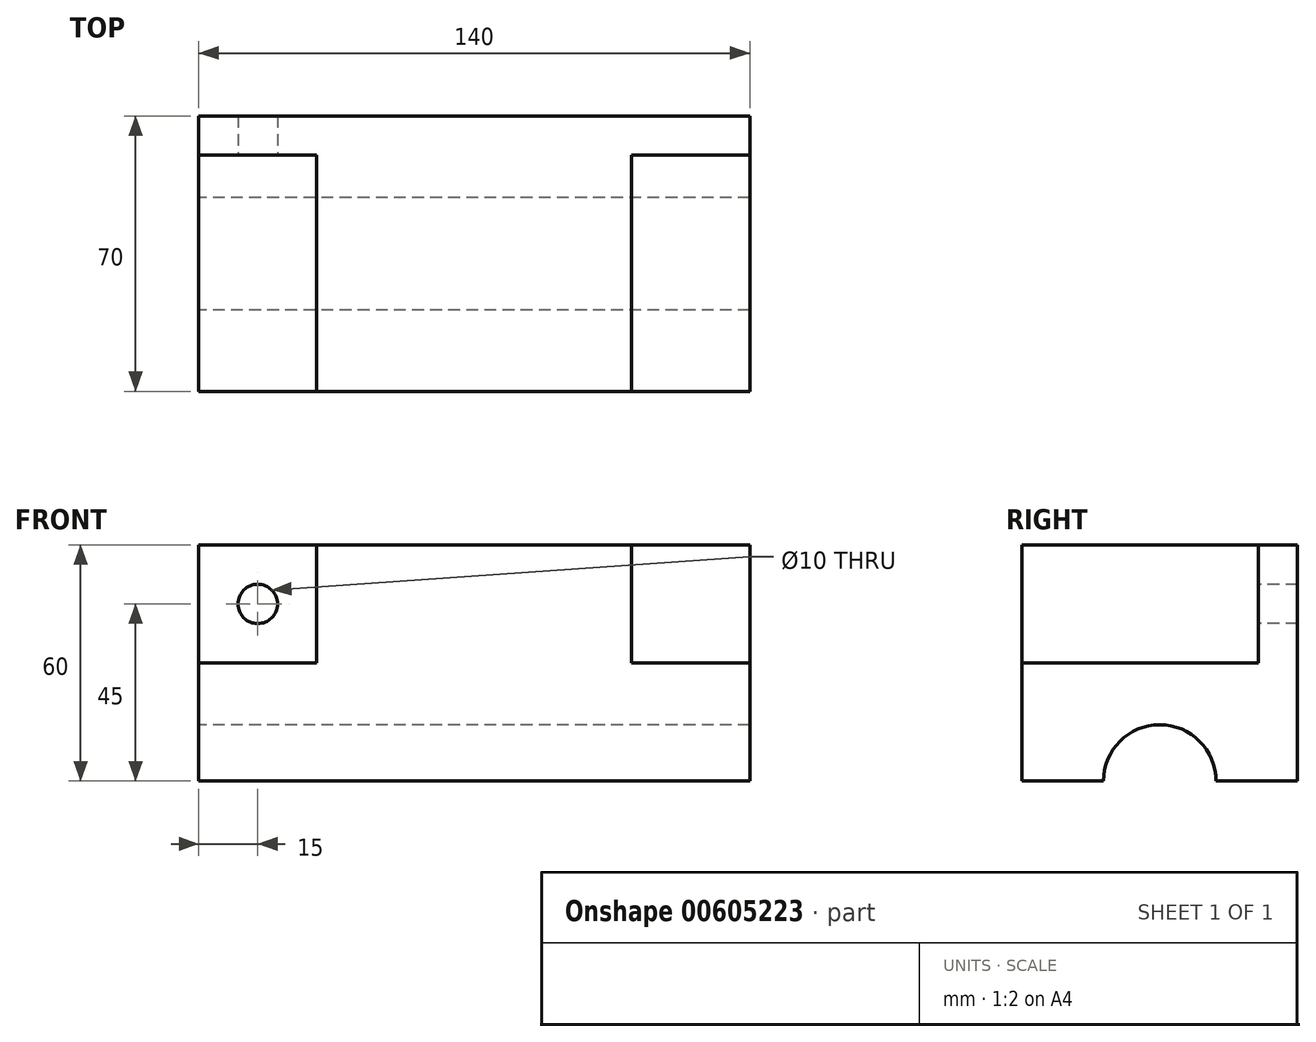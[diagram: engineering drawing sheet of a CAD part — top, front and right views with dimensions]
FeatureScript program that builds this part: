
annotation { "Feature Type Name" : "Feature", "Feature Type Description" : "" }
export const myFeature = defineFeature(function(context is Context, id is Id, definition is map)
    precondition{}
    {
        {
            var Q0;
            Q0=qCreatedBy(makeId("Right.planeOp"),FACE);
            var sketch = newSketch(context, id + "F0", { "sketchPlane" : qUnion([Q0])});
            skLineSegment(sketch, "E0", {"start": v(0, 0) * mm, "end": v(0, 30) * mm});
            skLineSegment(sketch, "E1", {"start": v(0, 30) * mm, "end": v(10, 30) * mm});
            skLineSegment(sketch, "E2", {"start": v(10, 30) * mm, "end": v(10, -30) * mm});
            skLineSegment(sketch, "E3", {"start": v(10, -30) * mm, "end": v(-60, -30) * mm});
            skLineSegment(sketch, "E4", {"start": v(-60, -30) * mm, "end": v(-60, 0) * mm});
            skLineSegment(sketch, "E5", {"start": v(-60, 0) * mm, "end": v(0, 0) * mm});
            skSolve(sketch);
        }
        {
            var Q0;
            Q0=makeQuery(id+"F0.imprint","IMPRINT",FACE,{"disambiguationData":[TD([[makeQuery(id+"F0.imprint","IMPRINT",EDGE,{"derivedFrom":sQuery(id+"F0.wireOp",EDGE,"E0")}),-1.0]])]});
            extrude(context, id + "F1", {"entities" : qUnion([Q0]), "oppositeDirection" : true, "depth" : 140 * mm, "offsetDistance" : 25 * mm, "symmetric" : true});
        }
        {
            var Q0;
            Q0=qCreatedBy(makeId("Right.planeOp"),FACE);
            var sketch = newSketch(context, id + "F2", { "sketchPlane" : qUnion([Q0])});
            skCircle(sketch, "E6", {"center": v(-25, -30) * mm, "radius": 14.3 * mm});
            skSolve(sketch);
        }
        {
            var Q0;
            Q0=makeQuery(id+"F2.imprint","IMPRINT",FACE,{"disambiguationData":[TD([[makeQuery(id+"F2.imprint","IMPRINT",EDGE,{"derivedFrom":sQuery(id+"F2.wireOp",EDGE,"E6")}),1.0]])]});
            extrude(context, id + "F3", {"entities" : qUnion([Q0]), "operationType" : NewBodyOperationType.REMOVE, "depth" : 175.4 * mm, "offsetDistance" : 25 * mm, "symmetric" : true});
        }
        {
            var Q0;
            Q0=qCreatedBy(makeId("Front.planeOp"),FACE);
            var sketch = newSketch(context, id + "F4", { "sketchPlane" : qUnion([Q0])});
            skLineSegment(sketch, "E7", {"start": v(0, 0) * mm, "end": v(40, 0) * mm});
            skLineSegment(sketch, "E8", {"start": v(40, 0) * mm, "end": v(40, 30) * mm});
            skLineSegment(sketch, "E9", {"start": v(40, 30) * mm, "end": v(0, 30) * mm});
            skLineSegment(sketch, "E10", {"start": v(0, 30) * mm, "end": v(0, 0) * mm});
            skLineSegment(sketch, "E11.MirrorCS", {"start": v(-40, 0) * mm, "end": v(-40, 30) * mm});
            skSolve(sketch);
        }
        {
            var Q0;
            Q0 = qSketchRegion(id + "F4", true);
            extrude(context, id + "F5", {"entities" : qUnion([Q0]), "operationType" : NewBodyOperationType.ADD, "depth" : 60 * mm, "offsetDistance" : 25 * mm});
        }
        {
            var Q0;
            Q0=makeQuery(id+"F1.opExtrude","SWEPT_BODY",BODY,{"disambiguationData":[OSD([sQuery(id+"F0.wireOp",EDGE,"E0"),sQuery(id+"F0.wireOp",EDGE,"E1"),sQuery(id+"F0.wireOp",EDGE,"E2"),sQuery(id+"F0.wireOp",EDGE,"E3"),sQuery(id+"F0.wireOp",EDGE,"E4"),sQuery(id+"F0.wireOp",EDGE,"E5")])]});
            var Q1;
            Q1=qCreatedBy(makeId("Right.planeOp"),FACE);
            mirror(context, id + "F6", {"operationType" : NewBodyOperationType.ADD, "entities" : qUnion([Q0]), "mirrorPlane" : qUnion([Q1])});
        }
        {
            var Q0;
            {var subQ2=sQuery(id+"F0.wireOp",EDGE,"E0");Q0=makeQuery(id+"F5.boolean.opBoolean","SPLIT",FACE,{"disambiguationData":[TD([makeQuery(id+"F5.opExtrude","SWEPT_FACE",FACE,{"disambiguationData":[OSD([sQuery(id+"F4.wireOp",EDGE,"E10")])]})])],"derivedFrom":makeQuery(id+"F1.opExtrude","SWEPT_FACE",FACE,{"disambiguationData":[OSD([subQ2])]})});}
            var sketch = newSketch(context, id + "F7", { "sketchPlane" : qUnion([Q0])});
            skCircle(sketch, "E12", {"center": v(-55, 15) * mm, "radius": 5 * mm});
            skSolve(sketch);
        }
        {
            var Q0;
            Q0=makeQuery(id+"F7.imprint","IMPRINT",FACE,{"disambiguationData":[TD([[makeQuery(id+"F7.imprint","IMPRINT",EDGE,{"derivedFrom":sQuery(id+"F7.wireOp",EDGE,"E12")}),1.0]])]});
            extrude(context, id + "F8", {"entities" : qUnion([Q0]), "operationType" : NewBodyOperationType.REMOVE, "oppositeDirection" : true, "depth" : 86.3 * mm, "offsetDistance" : 25 * mm});
        }
    });
